# Revit family: PRD_AR_ShwrHds_ShowerHead_SHAC0011_SHAC0013
name_source: partatom
category: Plumbing Fixtures
revit_build: Autodesk Revit 2018 (Build: 20190510_1515(x64)
units: mm (PartAtom-declared; Revit-internal decimal feet)

## family parameters
Cut with Voids When Loaded = Yes
Host = Face
OmniClass Number = 23.45.05.14.17
OmniClass Title = Showers
Part Type = Normal
Room Calculation Point = No
Round Connector Dimension = Use Diameter
Shared = Yes

## types (2) — shared parameters
AdjustableTiltAngle = Yes
AssetType = Fixed
Category = Pr_40_20_87_76, Shower heads
Default Elevation = 2000 mm  [stored 6.56168 ft]
DurationUnit = year
Features = diameter 26 mm, high-polished chrome-plated brass
Flow = 0.2 L/s
GrossWeight = 0.97 kg
HasTray = FALSE
IfcExportAs = IfcSanitaryTerminalType
IfcExportType = SHOWER
InletSize = DN 15
Manufacturer = KWC Group AG
ManufacturerName = KWC Group AG
ManufacturerURL = www.kwc.com
NBSDescription = Shower heads
NBSReference = 45-35-70/333
NetWeight = 0.90 kg
NominalWidth = 94 mm  [stored 0.308399 ft]
ProductInformation = https://pim.kwc.com
ShowerMaterial = PRD_AR_ChromatedBrass_HighPolished
ShowerType = Individual
Type = Shower head
TypeOfShowerHead = Spray shower head
URL = www.kwc.com
Uniclass2015Code = Pr_40_20_87_76
Uniclass2015Title = Shower heads
Uniclass2015Version = Products v1.17
Version = 1
WarrantyDurationUnit = year

## per-type parameters (varying)
| type | BIMObjectName | Color | Description | DiameterNominal | DrainSize | Finish | Material | ModelNumber | Name | NominalDepth | NominalHeight | ProductCode | ShowerHeadDescription | Size | TypeOfConnection |
| SHAC0013 | PRD_AR_ShowerHeads_AQUAJETShowerHead_SHAC0013 | Chrome | AQUAJET-Comfort DN 15 shower head with plastic jet face continuously adjustable between 13-23°, anti-limescale system and low aerosol formation. For wall connector with insertable connecting nozzle, diameter 26 mm, high-polished chrome-plated brass housing, with integrated flow regulator 9.0 l/min, ready for installation of anti-twist protection. Also suitable for shower trays, 800 x 800 mm. | 15  [stored 0.0492126 ft] | 15 mm  [stored 0.0492126 ft] | high-polished chrome | brass | 2030055724 | AQUAJET-Comfort Shower head SHAC0013 | 0 mm  [stored 0 ft] | 0 mm  [stored 0 ft] | 210.0588.387 | Shower head |  | Wall connection |
| SHAC0011 | PRD_AR_ShowerHeads_ShowerHead_SHAC0011 |  | AQUAJET-Comfort shower head with plastic jet face continuously adjustable between 13-23°, anti-limescale system and low aerosol formation. For installation on KWC shower panels with DN 15 connecting nozzles, diameter 26 mm, high-polished chrome-plated brass. | 0  [stored 0 ft] | 0 mm  [stored 0 ft] | high-polished | chrome-plated brass | 2030054254 | Shower Head SHAC0011 | 141 mm | 73 mm  [stored 0.239501 ft] |  | Spray shower head | 94 x 73 x 141 mm (W x H x D) | Panel |

note: column(s) folded — value = type name in every type: Model, ModelReference

note: [stored X ft] marks values corroborated as IEEE doubles in the binary element streams (Revit-internal decimal feet)

## geometry (parser evidence)
native form markers: Sweep x2
no freeform markers — native parametric forms only
